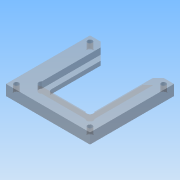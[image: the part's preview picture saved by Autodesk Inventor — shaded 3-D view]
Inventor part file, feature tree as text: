
AUTODESK INVENTOR PART (.ipt)
format: ipt  version: 2016 (Build 200138000, 138)  size: 147,968 bytes
history: native  units: mm
features: sketch x3, extrude x2, fillet x1, chamfer x1, hole x1
ambient origin geometry x8: Origin, YZ Plane, XZ Plane, XY Plane, X Axis, Y Axis, Z Axis, Center Point
bodies: Volumenkörper1 (feature_tree)
feature tree (8):
  extrude  "Extrusion1"  Depth=80.0mm
  extrude  "Extrusion2"  Depth=6.0mm
  fillet  "Rundung1"  Radius=2.12132mm
  chamfer  "Fase1"  Distance=50.0mm
  hole  "Bohrung1"  [1 undecoded]
  sketch  "Skizze1"  dims[d0=40.0mm d1=80.0mm]
  sketch  "Skizze2"  dims[d2=10.0mm d3=0.0mm d5=6.0mm d7=2.12132mm]
  sketch  "Skizze3"  dims[d8=2.12132mm d9=50.0mm d11=5.0mm d12=5.0mm d13=6.0mm d14=0.0mm d15=3.0mm d16=10.0mm d17=2.0mm d18=45.0deg d22=5.0mm d23=5.0mm d24=5.0mm d25=5.0mm d26=4.5mm d27=6.0mm d28=10.0mm d29=2.0mm d30=90.0deg d31=8.0mm d32=20.594885mm d33=70.0mm d34=70.0mm]
note: 1 required parameter value undecoded (feature->parameter linkage not recoverable at this tier; creation-order binding heuristic only, values carry confidence <= 0.55)
